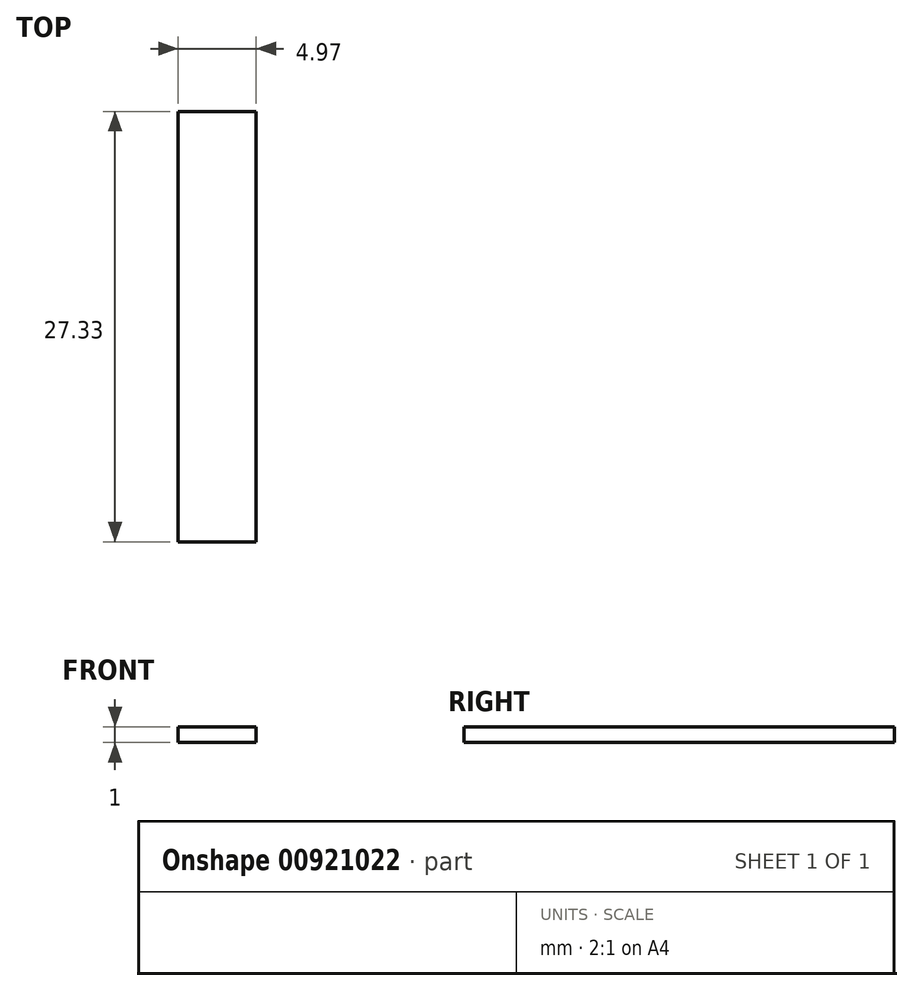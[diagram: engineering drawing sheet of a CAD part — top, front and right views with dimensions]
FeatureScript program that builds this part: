
annotation { "Feature Type Name" : "Feature", "Feature Type Description" : "" }
export const myFeature = defineFeature(function(context is Context, id is Id, definition is map)
    precondition{}
    {
        {
            var Q0;
            Q0=qCreatedBy(makeId("Top.planeOp"),FACE);
            var sketch = newSketch(context, id + "F0", { "sketchPlane" : qUnion([Q0])});
            skLineSegment(sketch, "E0.bottom", {"start": v(-52.17, 35.65) * mm, "end": v(-47.2, 35.65) * mm});
            skLineSegment(sketch, "E0.top", {"start": v(-52.17, 8.32) * mm, "end": v(-47.2, 8.32) * mm});
            skLineSegment(sketch, "E0.left", {"start": v(-52.17, 35.65) * mm, "end": v(-52.17, 8.32) * mm});
            skLineSegment(sketch, "E0.right", {"start": v(-47.2, 35.65) * mm, "end": v(-47.2, 8.32) * mm});
            skSolve(sketch);
        }
        {
            var Q0;
            Q0=makeQuery(id+"F0.imprint","IMPRINT",FACE,{"disambiguationData":[TD([[makeQuery(id+"F0.imprint","IMPRINT",EDGE,{"derivedFrom":sQuery(id+"F0.wireOp",EDGE,"E0.bottom")}),-1.0]])]});
            extrude(context, id + "F1", {"entities" : qUnion([Q0]), "depth" : 1 * mm, "offsetDistance" : 25 * mm});
        }
    });
